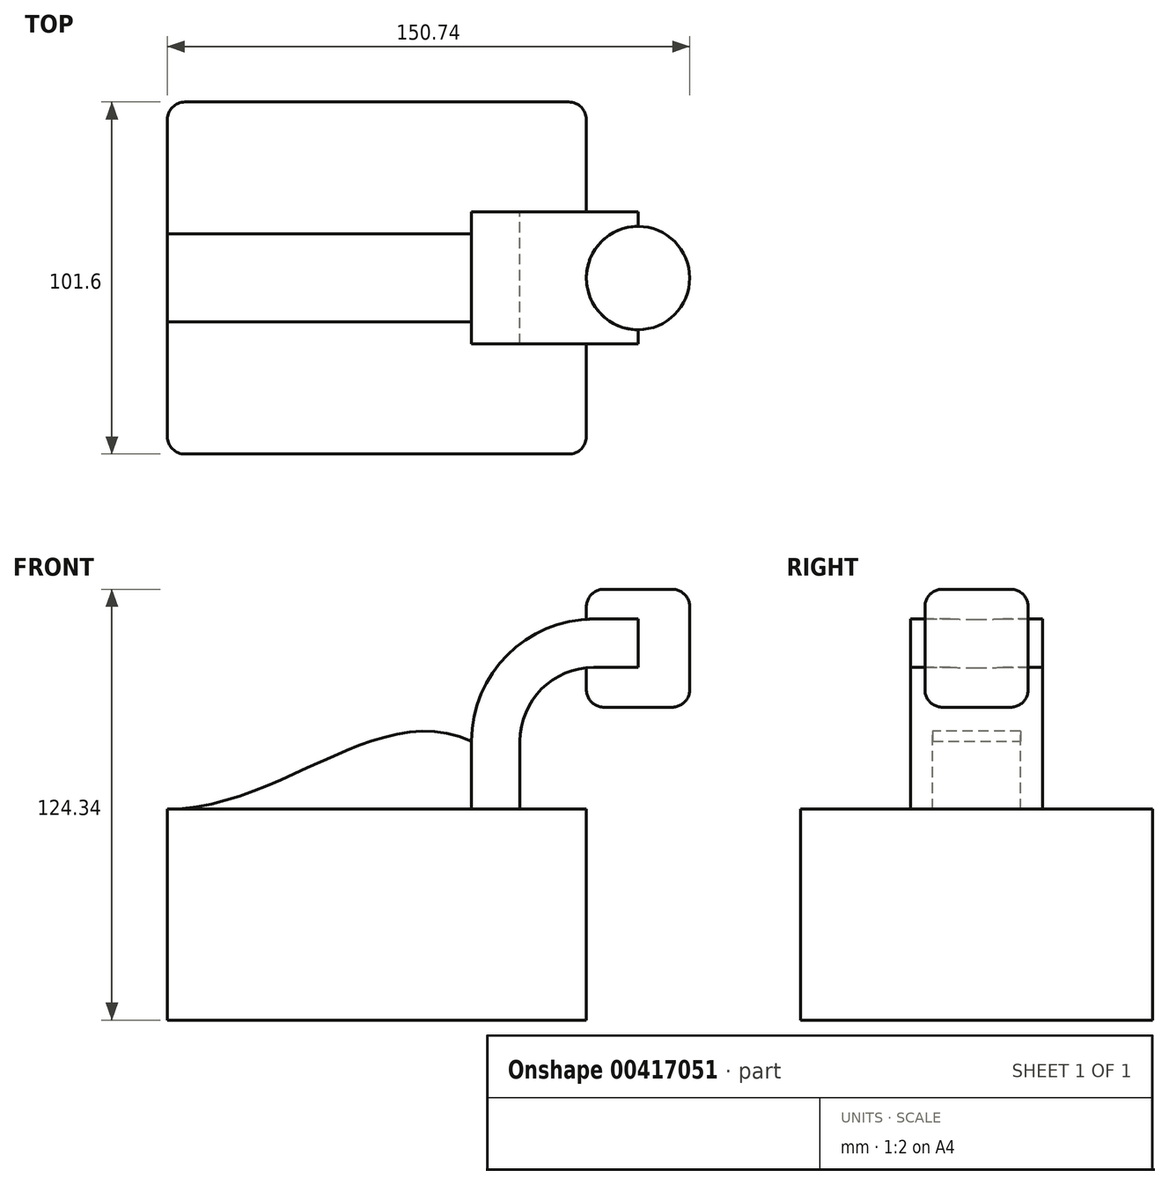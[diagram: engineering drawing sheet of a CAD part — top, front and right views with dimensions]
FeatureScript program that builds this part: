
annotation { "Feature Type Name" : "Feature", "Feature Type Description" : "" }
export const myFeature = defineFeature(function(context is Context, id is Id, definition is map)
    precondition{}
    {
        {
            var Q0;
            Q0=qCreatedBy(makeId("Front.planeOp"),FACE);
            var sketch = newSketch(context, id + "F0", { "sketchPlane" : qUnion([Q0])});
            skLineSegment(sketch, "E0.bottom", {"start": v(-60.47, -30.45) * mm, "end": v(60.47, -30.45) * mm});
            skLineSegment(sketch, "E0.top", {"start": v(-60.47, 30.45) * mm, "end": v(60.47, 30.45) * mm});
            skLineSegment(sketch, "E0.left", {"start": v(-60.47, -30.45) * mm, "end": v(-60.47, 30.45) * mm});
            skLineSegment(sketch, "E0.right", {"start": v(60.47, -30.45) * mm, "end": v(60.47, 30.45) * mm});
            skPoint(sketch, "E0.middle", {"position": v(0, 0) * mm});
            skLineSegment(sketch, "E1.bottom", {"start": v(60.47, 59.83) * mm, "end": v(90.27, 59.83) * mm});
            skLineSegment(sketch, "E1.top", {"start": v(60.47, 93.9) * mm, "end": v(90.27, 93.9) * mm});
            skLineSegment(sketch, "E1.left", {"start": v(60.47, 59.83) * mm, "end": v(60.47, 93.9) * mm});
            skLineSegment(sketch, "E1.right", {"start": v(90.27, 59.83) * mm, "end": v(90.27, 93.9) * mm});
            skPoint(sketch, "E1.middle", {"position": v(75.37, 76.86) * mm});
            skLineSegment(sketch, "E2", {"start": v(41.3, 30.45) * mm, "end": v(41.3, 50.03) * mm});
            skArc(sketch, "E3", {"start": v(41.3, 50.03) * mm, "mid": v(47.54, 65.08) * mm, "end": v(62.58, 71.31) * mm});
            skLineSegment(sketch, "E4", {"start": v(62.58, 71.31) * mm, "end": v(75.37, 71.31) * mm});
            skLineSegment(sketch, "E5.0", {"start": v(62.58, 85.28) * mm, "end": v(75.37, 85.28) * mm});
            skArc(sketch, "E5.1", {"start": v(27.33, 50.03) * mm, "mid": v(37.66, 74.96) * mm, "end": v(62.58, 85.28) * mm});
            skLineSegment(sketch, "E5.2", {"start": v(27.33, 30.45) * mm, "end": v(27.33, 50.03) * mm});
            skLineSegment(sketch, "E6", {"start": v(75.37, 59.83) * mm, "end": v(75.37, 93.9) * mm});
            skFitSpline(sketch, "E7", {"points": [v(-60.47, 30.45) * mm, v(27.33, 50.03) * mm], "startDerivative": vector(99.58, 0) * mm, "endDerivative": vector(82, -37.48) * mm});
            skSolve(sketch);
        }
        {
            var Q0;
            Q0=makeQuery(id+"F0.imprint","IMPRINT",FACE,{"disambiguationData":[TD([[makeQuery(id+"F0.imprint","IMPRINT",EDGE,{"derivedFrom":sQuery(id+"F0.wireOp",EDGE,"E0.bottom")}),1.0]])]});
            extrude(context, id + "F1", {"entities" : qUnion([Q0]), "endBound" : BoundingType.SYMMETRIC, "depth" : 101.6 * mm});
        }
        {
            var Q0;
            {var subQ1=sQuery(id+"F0.wireOp",EDGE,"E2");Q0=makeQuery(id+"F0.imprint","IMPRINT",FACE,{"disambiguationData":[TD([[makeQuery(id+"F0.imprint","IMPRINT",EDGE,{"derivedFrom":subQ1}),1.0]])]});}
            extrude(context, id + "F2", {"entities" : qUnion([Q0]), "operationType" : NewBodyOperationType.ADD, "endBound" : BoundingType.SYMMETRIC, "depth" : 38.1 * mm});
        }
        {
            var Q0;
            {var subQ1=sQuery(id+"F0.wireOp",EDGE,"E4");Q0=makeQuery(id+"F0.imprint","IMPRINT",FACE,{"disambiguationData":[TD([[makeQuery(id+"F0.imprint","IMPRINT",EDGE,{"derivedFrom":subQ1}),1.0]])]});}
            extrude(context, id + "F3", {"entities" : qUnion([Q0]), "operationType" : NewBodyOperationType.ADD, "endBound" : BoundingType.SYMMETRIC, "depth" : 38.1 * mm});
        }
        {
            var Q0;
            {var subQ0=sQuery(id+"F0.wireOp",EDGE,"E1.right");Q0=makeQuery(id+"F0.imprint","IMPRINT",FACE,{"disambiguationData":[TD([[makeQuery(id+"F0.imprint","IMPRINT",EDGE,{"derivedFrom":subQ0}),1.0]])]});}
            var Q1;
            Q1=sQuery(id+"F0.wireOp",EDGE,"E6");
            revolve(context, id + "F4", {"operationType" : NewBodyOperationType.ADD, "entities" : qUnion([Q0]), "axis" : qUnion([Q1]), "revolveType" : RevolveType.FULL});
        }
        {
            var Q0;
            Q0=makeQuery(id+"F1.opExtrude","CAP_EDGE",EDGE,{"disambiguationData":[OSD([sQuery(id+"F0.wireOp",EDGE,"E0.right")])],"isStart":false});
            var Q1;
            Q1=makeQuery(id+"F1.opExtrude","CAP_EDGE",EDGE,{"disambiguationData":[OSD([sQuery(id+"F0.wireOp",EDGE,"E0.right")])],"isStart":true});
            var Q2;
            Q2=makeQuery(id+"F1.opExtrude","CAP_EDGE",EDGE,{"disambiguationData":[OSD([sQuery(id+"F0.wireOp",EDGE,"E0.left")])],"isStart":true});
            var Q3;
            Q3=makeQuery(id+"F1.opExtrude","CAP_EDGE",EDGE,{"disambiguationData":[OSD([sQuery(id+"F0.wireOp",EDGE,"E0.left")])],"isStart":false});
            fillet(context, id + "F5", {"entities" : qUnion([Q0, Q1, Q2, Q3]), "radius" : 5.08 * mm, "tangentPropagation" : true, "allowEdgeOverflow" : false});
        }
        {
            var Q0;
            Q0=makeQuery(id+"F4.opRevolve","SWEPT_EDGE",EDGE,{"disambiguationData":[OSD([sQuery(id+"F0.wireOp",EDGE,"E1.top"),sQuery(id+"F0.wireOp",EDGE,"E1.right")])]});
            var Q1;
            Q1=makeQuery(id+"F4.opRevolve","SWEPT_EDGE",EDGE,{"disambiguationData":[OSD([sQuery(id+"F0.wireOp",EDGE,"E1.bottom"),sQuery(id+"F0.wireOp",EDGE,"E1.right")])]});
            fillet(context, id + "F6", {"entities" : qUnion([Q0, Q1]), "radius" : 5.08 * mm, "tangentPropagation" : true, "allowEdgeOverflow" : false});
        }
        {
            var Q0;
            {var subQ2=sQuery(id+"F0.wireOp",EDGE,"E5.2");Q0=makeQuery(id+"F0.imprint","IMPRINT",FACE,{"disambiguationData":[TD([[makeQuery(id+"F0.imprint","IMPRINT",EDGE,{"derivedFrom":subQ2}),1.0]])]});}
            extrude(context, id + "F7", {"entities" : qUnion([Q0]), "operationType" : NewBodyOperationType.ADD, "endBound" : BoundingType.SYMMETRIC, "depth" : 25.4 * mm});
        }
    });
